# Revit family: Tub_Spout-Grohe-Plus-13407_Series
name_source: partatom
category: Plumbing Fixtures
revit_build: Autodesk Revit 2018 (Build: 20170223_1515(x64)
units: mm (PartAtom-declared; Revit-internal decimal feet)

## family parameters
Cut with Voids When Loaded = No
Host = Face
OmniClass Number = 23.45.05.14.21.11
OmniClass Title = Bath/Shower Units
Part Type = Normal
Room Calculation Point = No
Round Connector Dimension = Use Diameter
Shared = Yes

## types (2) — shared parameters
Assembly Code = D2020300
CW Connection = No
CWFU = 3
Compliance Certifications = • Energy Policy Act of 1992,• ASME A112.18.1/CSA B125.1,• LOGO CEC
Default Elevation = 21"
Description = Tub Spout
HW Connection = No
HWFU = 3
Height = 2 5/16"
Installation Type = Wall Mounted
Length = 8 9/16"
Manufacturer = Grohe
Product Documentation Link = https://americanstandard.box.com
Product Page URL = https://www.grohe.us
Tempered Connection Diameter = 1/2"
Tempered Water Connection = Yes
URL = https://www.grohe.us
Vent Connection = No
WFU = 4
Waste Connection = No
Width = 2 11/16"
cUPC Compliant = Yes

## per-type parameters (varying)
| type | Finish | Material |
| 13407EN3 | Metal-Grohe-EN3-Brushed Nickel Infinity Finish | Metal-Grohe-EN3-Brushed Nickel Infinity Finish |
| 13407003 | Metal-Grohe-003-StarLight Chrome | Metal-Grohe-003-StarLight Chrome |

note: column(s) folded — value = type name in every type: Model

## geometry (parser evidence)
native form markers: Sweep x3
no freeform markers — native parametric forms only
